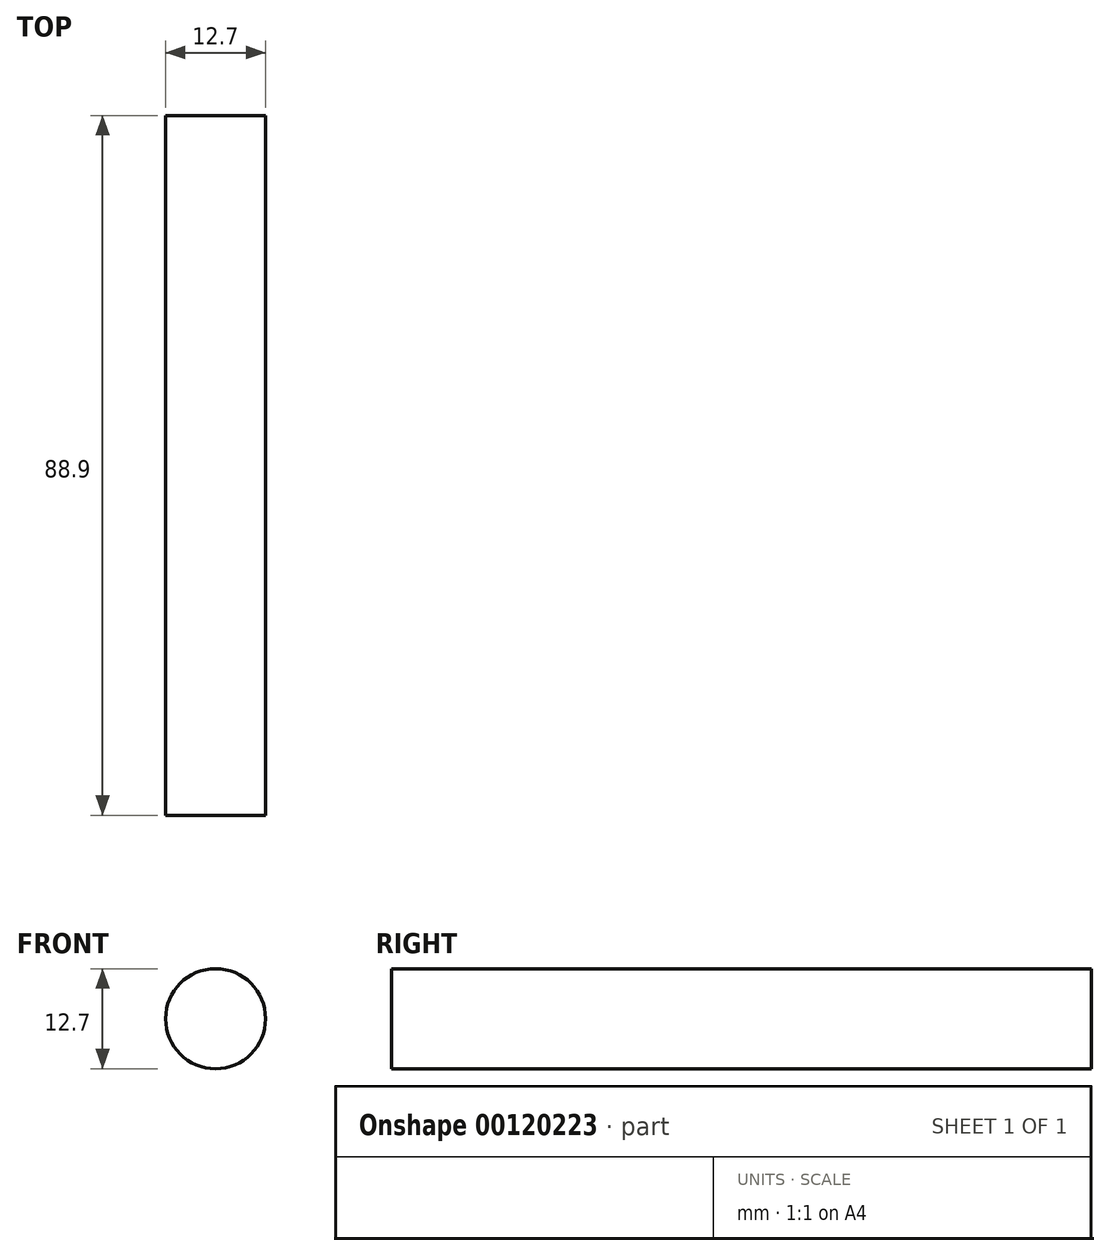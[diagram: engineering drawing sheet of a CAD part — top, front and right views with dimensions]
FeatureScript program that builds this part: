
annotation { "Feature Type Name" : "Feature", "Feature Type Description" : "" }
export const myFeature = defineFeature(function(context is Context, id is Id, definition is map)
    precondition{}
    {
        {
            var Q0;
            Q0=qCreatedBy(makeId("Front.planeOp"),FACE);
            var sketch = newSketch(context, id + "F0", { "sketchPlane" : qUnion([Q0])});
            skCircle(sketch, "E0", {"center": v(0, 0) * mm, "radius": 6.35 * mm});
            skSolve(sketch);
        }
        {
            var Q0;
            Q0 = qSketchRegion(id + "F0", true);
            extrude(context, id + "F1", {"entities" : qUnion([Q0]), "endBound" : BoundingType.SYMMETRIC, "depth" : 88.9 * mm});
        }
    });
